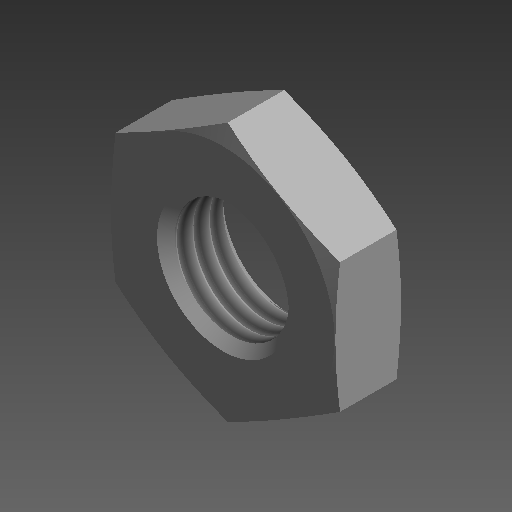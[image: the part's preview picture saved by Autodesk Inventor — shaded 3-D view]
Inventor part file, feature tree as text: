
AUTODESK INVENTOR PART (.ipt)
format: ipt  version: 2021 (Build 250183000, 183)  size: 136,192 bytes
history: native  units: mm (DEFAULTED — no unit token found)
features: other x14, sketch x3, revolve x2, extrude x1, thread x1
ambient origin geometry x8: Origin, YZ Plane, XZ Plane, XY Plane, X Axis, Y Axis, Z Axis, Center Point
bodies: Solid1 (feature_tree)
feature tree (21):
  revolve  "Revolution1"  [1 undecoded]
  extrude  "Extrusion1"  Depth=3.647mm TaperAngle=0.0deg
  revolve  "Revolution2"  [1 undecoded]
  thread  "Thread1"  [1 undecoded]
  other  "2CYL_XY"
  other  "2CYL_YZ"
  other  "2CYL_ZX"
  other  "2CYL_X"
  other  "2CYL_Y"
  other  "2CYL_Z"
  other  "2CYL_Center"
  other  "din439b_punkt_XY"
  other  "din439b_punkt_YZ"
  other  "din439b_punkt_ZX"
  other  "din439b_punkt_X"
  other  "din439b_punkt_Y"
  other  "din439b_punkt_Z"
  other  "din439b_punkt_Center"
  sketch  "Sketch_1"  dims[d0=360.0deg d1=12.0mm d2=0.0mm]
  sketch  "Sketch_2"  dims[d3=360.0deg d4=3.647mm d5=0.0mm]
  sketch  "Sketch_3"  dims[d6=0.0mm]
note: 3 required parameter values undecoded (feature->parameter linkage not recoverable at this tier; creation-order binding heuristic only, values carry confidence <= 0.55)